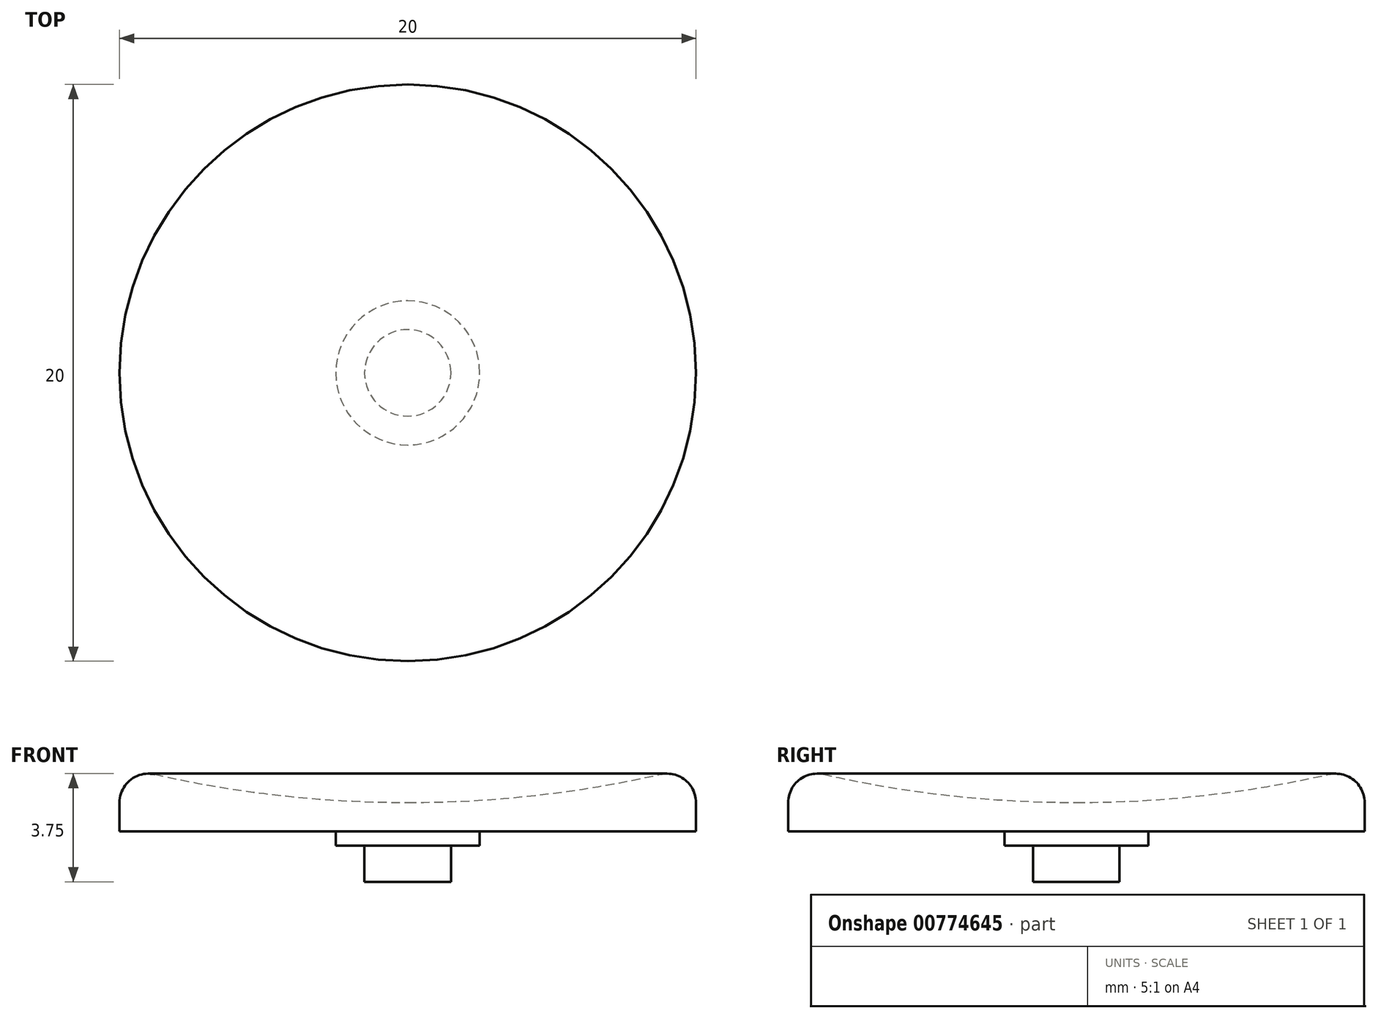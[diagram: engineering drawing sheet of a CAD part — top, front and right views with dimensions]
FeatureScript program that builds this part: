
annotation { "Feature Type Name" : "Feature", "Feature Type Description" : "" }
export const myFeature = defineFeature(function(context is Context, id is Id, definition is map)
    precondition{}
    {
        {
            var Q0;
            Q0=qCreatedBy(makeId("Front.planeOp"),FACE);
            var sketch = newSketch(context, id + "F0", { "sketchPlane" : qUnion([Q0])});
            skLineSegment(sketch, "E0", {"start": v(-3.5, 2.5) * mm, "end": v(-10, 2.5) * mm});
            skLineSegment(sketch, "E1", {"start": v(-10, 2.5) * mm, "end": v(-10, 3.5) * mm});
            skArc(sketch, "E2", {"start": v(-8.78, 4.48) * mm, "mid": v(-9.62, 4.28) * mm, "end": v(-10, 3.5) * mm});
            skArc(sketch, "E3", {"start": v(-8.78, 4.48) * mm, "mid": v(-4.42, 3.74) * mm, "end": v(0, 3.5) * mm});
            skPoint(sketch, "E4.orphan", {"position": v(0, 0) * mm});
            skLineSegment(sketch, "E5", {"start": v(-2.5, 2) * mm, "end": v(-1.5, 2) * mm});
            skLineSegment(sketch, "E6", {"start": v(-1.5, 2) * mm, "end": v(-1.5, 0.75) * mm});
            skLineSegment(sketch, "E7", {"start": v(-1.5, 0.75) * mm, "end": v(0, 0.75) * mm});
            skLineSegment(sketch, "E8", {"start": v(0, 0.75) * mm, "end": v(0, 3.5) * mm});
            skLineSegment(sketch, "E9", {"start": v(-2.5, 2) * mm, "end": v(-2.5, 2.5) * mm});
            skLineSegment(sketch, "E10", {"start": v(-2.5, 2.5) * mm, "end": v(-3.5, 2.5) * mm});
            skSolve(sketch);
        }
        {
            var Q0;
            Q0=qCreatedBy(makeId("Front.planeOp"),FACE);
            var sketch = newSketch(context, id + "F1", { "sketchPlane" : qUnion([Q0])});
            skLineSegment(sketch, "E11", {"start": v(0, -21.55) * mm, "end": v(0, 31.93) * mm});
            skSolve(sketch);
        }
        {
            var Q0;
            Q0=makeQuery(id+"F0.imprint","IMPRINT",FACE,{"disambiguationData":[TD([[makeQuery(id+"F0.imprint","IMPRINT",EDGE,{"derivedFrom":sQuery(id+"F0.wireOp",EDGE,"E0")}),-1.0]])]});
            var Q1;
            Q1=sQuery(id+"F1.wireOp",EDGE,"E11");
            revolve(context, id + "F2", {"surfaceOperationType" : NewSurfaceOperationType.NEW, "entities" : qUnion([Q0]), "axis" : qUnion([Q1]), "revolveType" : RevolveType.FULL});
        }
    });
